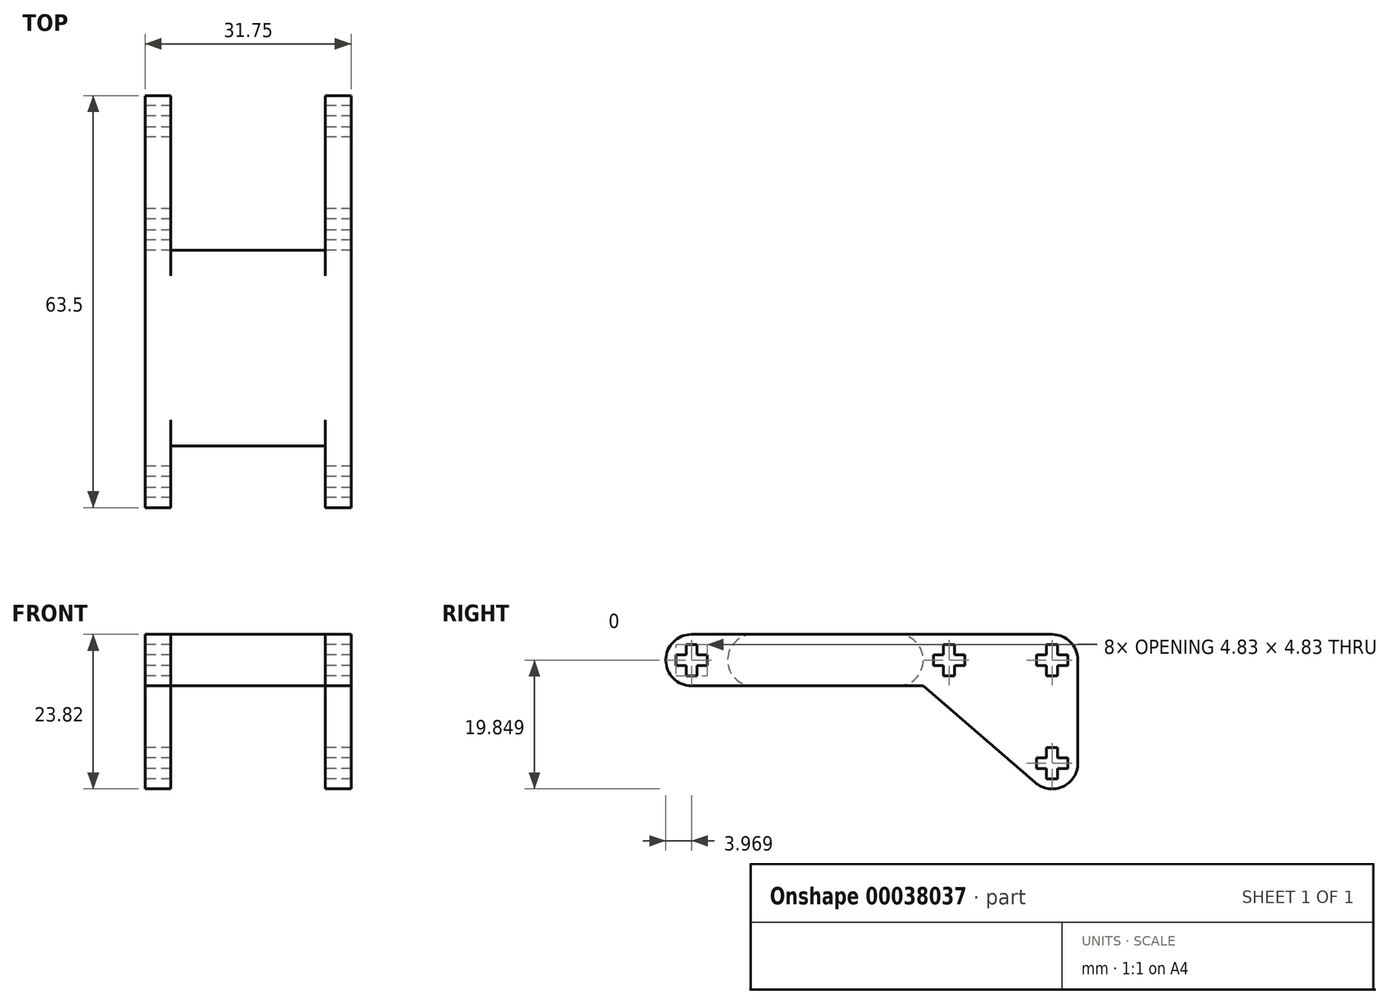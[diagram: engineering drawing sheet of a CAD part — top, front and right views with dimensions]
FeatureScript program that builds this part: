
annotation { "Feature Type Name" : "Feature", "Feature Type Description" : "" }
export const myFeature = defineFeature(function(context is Context, id is Id, definition is map)
    precondition{}
    {
        {
            var Q0;
            Q0=qCreatedBy(makeId("Top.planeOp"),FACE);
            var sketch = newSketch(context, id + "F0", { "sketchPlane" : qUnion([Q0])});
            skLineSegment(sketch, "E0.bottom", {"start": v(0, 0) * mm, "end": v(3.97, 0) * mm});
            skLineSegment(sketch, "E0.left", {"start": v(0, 0) * mm, "end": v(0, 63.5) * mm});
            skLineSegment(sketch, "E0.right", {"start": v(3.97, 0) * mm, "end": v(3.97, 9.53) * mm});
            skLineSegment(sketch, "E1.bottom", {"start": v(27.78, 0) * mm, "end": v(31.75, 0) * mm});
            skLineSegment(sketch, "E1.left", {"start": v(27.78, 0) * mm, "end": v(27.78, 9.53) * mm});
            skLineSegment(sketch, "E1.right", {"start": v(31.75, 0) * mm, "end": v(31.75, 63.5) * mm});
            skLineSegment(sketch, "E2", {"start": v(3.97, 9.53) * mm, "end": v(27.78, 9.53) * mm});
            skLineSegment(sketch, "E3", {"start": v(0, 63.5) * mm, "end": v(3.97, 63.5) * mm});
            skLineSegment(sketch, "E4", {"start": v(3.97, 63.5) * mm, "end": v(3.97, 39.69) * mm});
            skLineSegment(sketch, "E5", {"start": v(3.97, 39.69) * mm, "end": v(27.78, 39.69) * mm});
            skLineSegment(sketch, "E6", {"start": v(27.78, 39.69) * mm, "end": v(27.78, 63.5) * mm});
            skLineSegment(sketch, "E7", {"start": v(27.78, 63.5) * mm, "end": v(31.75, 63.5) * mm});
            skSolve(sketch);
        }
        {
            var Q0;
            Q0=qSketchRegion(id+"F0",true);
            extrude(context, id + "F1", {"entities" : qUnion([Q0]), "depth" : 7.94 * mm});
        }
        {
            var Q0;
            Q0=makeQuery(id+"F1.opExtrude","CAP_EDGE",EDGE,{"disambiguationData":[OSD([sQuery(id+"F0.wireOp",EDGE,"E5")])],"isStart":false});
            var Q1;
            Q1=makeQuery(id+"F1.opExtrude","CAP_EDGE",EDGE,{"disambiguationData":[OSD([sQuery(id+"F0.wireOp",EDGE,"E5")])],"isStart":true});
            var Q2;
            Q2=makeQuery(id+"F1.opExtrude","CAP_EDGE",EDGE,{"disambiguationData":[OSD([sQuery(id+"F0.wireOp",EDGE,"E3")])],"isStart":false});
            var Q3;
            Q3=makeQuery(id+"F1.opExtrude","CAP_EDGE",EDGE,{"disambiguationData":[OSD([sQuery(id+"F0.wireOp",EDGE,"E7")])],"isStart":false});
            var Q4;
            Q4=makeQuery(id+"F1.opExtrude","CAP_EDGE",EDGE,{"disambiguationData":[OSD([sQuery(id+"F0.wireOp",EDGE,"E0.bottom")])],"isStart":false});
            var Q5;
            Q5=makeQuery(id+"F1.opExtrude","CAP_EDGE",EDGE,{"disambiguationData":[OSD([sQuery(id+"F0.wireOp",EDGE,"E0.bottom")])],"isStart":true});
            var Q6;
            Q6=makeQuery(id+"F1.opExtrude","CAP_EDGE",EDGE,{"disambiguationData":[OSD([sQuery(id+"F0.wireOp",EDGE,"E1.bottom")])],"isStart":false});
            var Q7;
            Q7=makeQuery(id+"F1.opExtrude","CAP_EDGE",EDGE,{"disambiguationData":[OSD([sQuery(id+"F0.wireOp",EDGE,"E1.bottom")])],"isStart":true});
            var Q8;
            Q8=makeQuery(id+"F1.opExtrude","CAP_EDGE",EDGE,{"disambiguationData":[OSD([sQuery(id+"F0.wireOp",EDGE,"E2")])],"isStart":false});
            var Q9;
            Q9=makeQuery(id+"F1.opExtrude","CAP_EDGE",EDGE,{"disambiguationData":[OSD([sQuery(id+"F0.wireOp",EDGE,"E2")])],"isStart":true});
            fillet(context, id + "F2", {"entities" : qUnion([Q0, Q1, Q2, Q3, Q4, Q5, Q6, Q7, Q8, Q9]), "radius" : 3.97 * mm, "tangentPropagation" : true, "allowEdgeOverflow" : false});
        }
        {
            var Q0;
            Q0=makeQuery(id+"F1.opExtrude","CAP_FACE",FACE,{"disambiguationData":[OSD([sQuery(id+"F0.wireOp",EDGE,"E0.bottom"),sQuery(id+"F0.wireOp",EDGE,"E0.left"),sQuery(id+"F0.wireOp",EDGE,"E0.right"),sQuery(id+"F0.wireOp",EDGE,"E1.bottom"),sQuery(id+"F0.wireOp",EDGE,"E1.left"),sQuery(id+"F0.wireOp",EDGE,"E1.right"),sQuery(id+"F0.wireOp",EDGE,"E2"),sQuery(id+"F0.wireOp",EDGE,"E3"),sQuery(id+"F0.wireOp",EDGE,"E4"),sQuery(id+"F0.wireOp",EDGE,"E5"),sQuery(id+"F0.wireOp",EDGE,"E6"),sQuery(id+"F0.wireOp",EDGE,"E7")])],"isStart":true});
            var sketch = newSketch(context, id + "F3", { "sketchPlane" : qUnion([Q0])});
            skLineSegment(sketch, "E8.bottom", {"start": v(31.75, -63.5) * mm, "end": v(27.78, -63.5) * mm});
            skLineSegment(sketch, "E8.top", {"start": v(31.75, -39.69) * mm, "end": v(27.78, -39.69) * mm});
            skLineSegment(sketch, "E8.left", {"start": v(31.75, -63.5) * mm, "end": v(31.75, -39.69) * mm});
            skLineSegment(sketch, "E8.right", {"start": v(27.78, -63.5) * mm, "end": v(27.78, -39.69) * mm});
            skLineSegment(sketch, "E9.bottom", {"start": v(3.97, -63.5) * mm, "end": v(0, -63.5) * mm});
            skLineSegment(sketch, "E9.top", {"start": v(3.97, -39.69) * mm, "end": v(0, -39.69) * mm});
            skLineSegment(sketch, "E9.left", {"start": v(3.97, -63.5) * mm, "end": v(3.97, -39.69) * mm});
            skLineSegment(sketch, "E9.right", {"start": v(0, -63.5) * mm, "end": v(0, -39.69) * mm});
            skSolve(sketch);
        }
        {
            var Q0;
            Q0=qSketchRegion(id+"F3",true);
            extrude(context, id + "F4", {"entities" : qUnion([Q0]), "operationType" : NewBodyOperationType.ADD, "depth" : 15.88 * mm});
        }
        {
            var Q0;
            Q0=makeQuery(id+"F1.opExtrude","SWEPT_FACE",FACE,{"disambiguationData":[OSD([sQuery(id+"F0.wireOp",EDGE,"E0.left")])]});
            var sketch = newSketch(context, id + "F5", { "sketchPlane" : qUnion([Q0])});
            skLineSegment(sketch, "E10.rect.bottom", {"start": v(-6.38, 3.12) * mm, "end": v(-1.56, 3.12) * mm});
            skLineSegment(sketch, "E10.rect.top", {"start": v(-6.38, 4.81) * mm, "end": v(-1.56, 4.81) * mm});
            skLineSegment(sketch, "E10.rect.left", {"start": v(-6.38, 3.12) * mm, "end": v(-6.38, 4.81) * mm});
            skLineSegment(sketch, "E10.rect.right", {"start": v(-1.56, 3.12) * mm, "end": v(-1.56, 4.81) * mm});
            skPoint(sketch, "E10.rect.middle", {"position": v(-3.97, 3.97) * mm});
            skLineSegment(sketch, "E11.rect.bottom", {"start": v(-3.12, 1.56) * mm, "end": v(-4.81, 1.56) * mm});
            skLineSegment(sketch, "E11.rect.top", {"start": v(-3.12, 6.38) * mm, "end": v(-4.81, 6.38) * mm});
            skLineSegment(sketch, "E11.rect.left", {"start": v(-3.12, 1.56) * mm, "end": v(-3.12, 6.38) * mm});
            skLineSegment(sketch, "E11.rect.right", {"start": v(-4.81, 1.56) * mm, "end": v(-4.81, 6.38) * mm});
            skLineSegment(sketch, "E12.bottom", {"start": v(-39.69, 0) * mm, "end": v(-63.5, 0) * mm, "construction": true});
            skLineSegment(sketch, "E12.top", {"start": v(-39.69, -15.87) * mm, "end": v(-63.5, -15.87) * mm});
            skLineSegment(sketch, "E12.left", {"start": v(-39.69, 0) * mm, "end": v(-39.69, -15.87) * mm});
            skLineSegment(sketch, "E12.right", {"start": v(-63.5, 0) * mm, "end": v(-63.5, -15.88) * mm});
            skArc(sketch, "E13", {"start": v(-63.5, -11.9) * mm, "mid": v(-61.18, -15.52) * mm, "end": v(-56.94, -14.9) * mm});
            skLineSegment(sketch, "E14", {"start": v(-39.69, 0) * mm, "end": v(-56.94, -14.9) * mm});
            skLineSegment(sketch, "E15.rect.bottom", {"start": v(-57.12, -11.06) * mm, "end": v(-61.94, -11.06) * mm});
            skLineSegment(sketch, "E15.rect.top", {"start": v(-57.12, -12.75) * mm, "end": v(-61.94, -12.75) * mm});
            skLineSegment(sketch, "E15.rect.left", {"start": v(-57.12, -11.06) * mm, "end": v(-57.12, -12.75) * mm});
            skLineSegment(sketch, "E15.rect.right", {"start": v(-61.94, -11.06) * mm, "end": v(-61.94, -12.75) * mm});
            skLineSegment(sketch, "E16.rect.bottom", {"start": v(-60.38, -9.5) * mm, "end": v(-58.69, -9.5) * mm});
            skLineSegment(sketch, "E16.rect.top", {"start": v(-60.38, -14.32) * mm, "end": v(-58.69, -14.32) * mm});
            skLineSegment(sketch, "E16.rect.left", {"start": v(-60.38, -9.5) * mm, "end": v(-60.38, -14.32) * mm});
            skLineSegment(sketch, "E16.rect.right", {"start": v(-58.69, -9.5) * mm, "end": v(-58.69, -14.32) * mm});
            skLineSegment(sketch, "E17.rect.bottom", {"start": v(-60.38, 6.38) * mm, "end": v(-58.69, 6.38) * mm});
            skLineSegment(sketch, "E17.rect.top", {"start": v(-60.38, 1.56) * mm, "end": v(-58.69, 1.56) * mm});
            skLineSegment(sketch, "E17.rect.left", {"start": v(-60.38, 6.38) * mm, "end": v(-60.38, 1.56) * mm});
            skLineSegment(sketch, "E17.rect.right", {"start": v(-58.69, 6.38) * mm, "end": v(-58.69, 1.56) * mm});
            skPoint(sketch, "E17.rect.middle", {"position": v(-59.53, 3.97) * mm});
            skLineSegment(sketch, "E18.rect.bottom", {"start": v(-61.94, 4.81) * mm, "end": v(-57.12, 4.81) * mm});
            skLineSegment(sketch, "E18.rect.top", {"start": v(-61.94, 3.12) * mm, "end": v(-57.12, 3.12) * mm});
            skLineSegment(sketch, "E18.rect.left", {"start": v(-61.94, 4.81) * mm, "end": v(-61.94, 3.12) * mm});
            skLineSegment(sketch, "E18.rect.right", {"start": v(-57.12, 4.81) * mm, "end": v(-57.12, 3.12) * mm});
            skLineSegment(sketch, "E19.rect.bottom", {"start": v(-44.5, 6.38) * mm, "end": v(-42.81, 6.38) * mm});
            skLineSegment(sketch, "E19.rect.top", {"start": v(-44.5, 1.56) * mm, "end": v(-42.81, 1.56) * mm});
            skLineSegment(sketch, "E19.rect.left", {"start": v(-44.5, 6.38) * mm, "end": v(-44.5, 1.56) * mm});
            skLineSegment(sketch, "E19.rect.right", {"start": v(-42.81, 6.38) * mm, "end": v(-42.81, 1.56) * mm});
            skPoint(sketch, "E19.rect.middle", {"position": v(-43.66, 3.97) * mm});
            skLineSegment(sketch, "E20.rect.bottom", {"start": v(-46.07, 4.81) * mm, "end": v(-41.24, 4.81) * mm});
            skLineSegment(sketch, "E20.rect.top", {"start": v(-46.07, 3.12) * mm, "end": v(-41.24, 3.12) * mm});
            skLineSegment(sketch, "E20.rect.left", {"start": v(-46.07, 4.81) * mm, "end": v(-46.07, 3.12) * mm});
            skLineSegment(sketch, "E20.rect.right", {"start": v(-41.24, 4.81) * mm, "end": v(-41.24, 3.12) * mm});
            skLineSegment(sketch, "E21", {"start": v(-43.66, 3.97) * mm, "end": v(-59.53, 3.97) * mm, "construction": true});
            skLineSegment(sketch, "E22", {"start": v(-59.53, 3.97) * mm, "end": v(-59.53, -11.9) * mm, "construction": true});
            skSolve(sketch);
        }
        {
            var Q0;
            Q0=qSketchRegion(id+"F5",true);
            var Q1;
            Q1=makeQuery(id+"F1.opExtrude","SWEPT_FACE",FACE,{"disambiguationData":[OSD([sQuery(id+"F0.wireOp",EDGE,"E1.right")])]});
            extrude(context, id + "F6", {"entities" : qUnion([Q0]), "operationType" : NewBodyOperationType.REMOVE, "endBound" : BoundingType.UP_TO_SURFACE, "oppositeDirection" : true, "endBoundEntityFace" : qUnion([Q1]), "depth" : 25.4 * mm});
        }
    });
